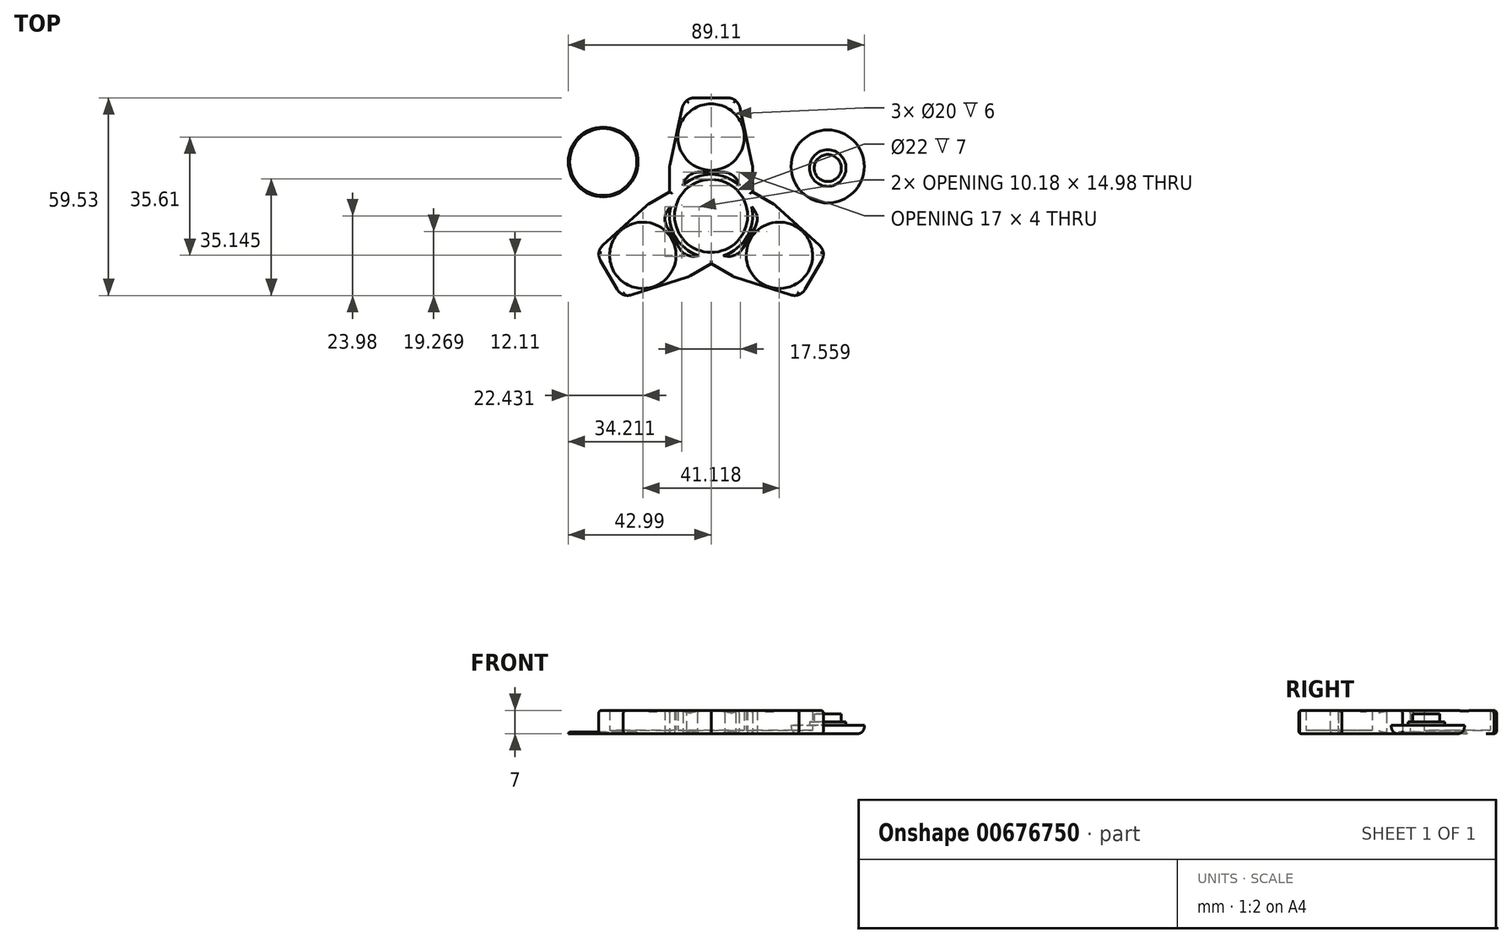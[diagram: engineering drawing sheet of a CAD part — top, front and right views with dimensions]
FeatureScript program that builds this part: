
annotation { "Feature Type Name" : "Feature", "Feature Type Description" : "" }
export const myFeature = defineFeature(function(context is Context, id is Id, definition is map)
    precondition{}
    {
        {
            var Q0;
            Q0=qCreatedBy(makeId("Top.planeOp"),FACE);
            var sketch = newSketch(context, id + "F0", { "sketchPlane" : qUnion([Q0])});
            skCircle(sketch, "E0", {"center": v(0, 0) * mm, "radius": 11 * mm});
            skCircle(sketch, "E1", {"center": v(0, 0) * mm, "radius": 12.5 * mm});
            skLineSegment(sketch, "E2", {"start": v(-8.5, 9.17) * mm, "end": v(-8.5, 13.17) * mm});
            skLineSegment(sketch, "E3", {"start": v(-8.5, 13.17) * mm, "end": v(8.5, 13.17) * mm});
            skLineSegment(sketch, "E4", {"start": v(8.5, 13.17) * mm, "end": v(8.5, 9.17) * mm});
            skLineSegment(sketch, "E5", {"start": v(-12.5, 0) * mm, "end": v(-12.5, 14.98) * mm});
            skLineSegment(sketch, "E6", {"start": v(12.5, 0) * mm, "end": v(12.5, 14.98) * mm});
            skLineSegment(sketch, "E7", {"start": v(0, 35.55) * mm, "end": v(8, 35.55) * mm});
            skPoint(sketch, "E7.startSnap0", {"position": v(0, 13.17) * mm});
            skLineSegment(sketch, "E8", {"start": v(0, 35.55) * mm, "end": v(-8, 35.55) * mm});
            skLineSegment(sketch, "E9", {"start": v(-8, 35.55) * mm, "end": v(-12.5, 14.98) * mm});
            skLineSegment(sketch, "E10", {"start": v(8, 35.55) * mm, "end": v(12.5, 14.98) * mm});
            skCircle(sketch, "E11", {"center": v(0, 23.74) * mm, "radius": 10 * mm});
            skSolve(sketch);
        }
        {
            var Q0;
            Q0=makeQuery(id+"F0.imprint","IMPRINT",FACE,{"disambiguationData":[TD([[makeQuery(id+"F0.imprint","IMPRINT",EDGE,{"derivedFrom":sQuery(id+"F0.wireOp",EDGE,"E0")}),-1.0]])]});
            extrude(context, id + "F1", {"entities" : qUnion([Q0]), "depth" : 7 * mm, "offsetDistance" : 25 * mm});
        }
        {
            var Q0;
            {var subQ4=sQuery(id+"F0.wireOp",EDGE,"E2");Q0=makeQuery(id+"F0.imprint","IMPRINT",FACE,{"disambiguationData":[TD([[makeQuery(id+"F0.imprint","IMPRINT",EDGE,{"derivedFrom":subQ4}),1.0]])]});}
            extrude(context, id + "F2", {"entities" : qUnion([Q0]), "depth" : 7 * mm, "offsetDistance" : 25 * mm});
        }
        {
            var Q0;
            Q0=makeQuery(id+"F0.imprint","IMPRINT",FACE,{"disambiguationData":[TD([[makeQuery(id+"F0.imprint","IMPRINT",EDGE,{"derivedFrom":sQuery(id+"F0.wireOp",EDGE,"E11")}),1.0]])]});
            extrude(context, id + "F3", {"entities" : qUnion([Q0]), "operationType" : NewBodyOperationType.ADD, "depth" : 1 * mm, "offsetDistance" : 25 * mm});
        }
        {
            var Q0;
            Q0=makeQuery(id+"F2.opExtrude","SWEPT_EDGE",EDGE,{"disambiguationData":[OSD([sQuery(id+"F0.wireOp",EDGE,"E7"),sQuery(id+"F0.wireOp",EDGE,"E10")])]});
            var Q1;
            Q1=makeQuery(id+"F2.opExtrude","SWEPT_EDGE",EDGE,{"disambiguationData":[OSD([sQuery(id+"F0.wireOp",EDGE,"E8"),sQuery(id+"F0.wireOp",EDGE,"E9")])]});
            chamfer(context, id + "F4", {"entities" : qUnion([Q0, Q1]), "width" : 2 * mm, "tangentPropagation" : true});
        }
        {
            var Q0;
            {var subQ0=sQuery(id+"F0.wireOp",EDGE,"E10");Q0=makeQuery(id+"F4.opChamfer","BLEND_EDGE",EDGE,{"blendedFrom":[makeQuery(id+"F2.opExtrude","SWEPT_EDGE",EDGE,{"disambiguationData":[OSD([sQuery(id+"F0.wireOp",EDGE,"E7"),subQ0])]}),makeQuery(id+"F2.opExtrude","SWEPT_FACE",FACE,{"disambiguationData":[OSD([subQ0])]})],"blendedInto":[makeQuery(id+"F2.opExtrude","SWEPT_FACE",FACE,{"disambiguationData":[OSD([subQ0])]})]});}
            var Q1;
            {var subQ0=sQuery(id+"F0.wireOp",EDGE,"E7");Q1=makeQuery(id+"F4.opChamfer","BLEND_EDGE",EDGE,{"blendedFrom":[makeQuery(id+"F2.opExtrude","SWEPT_EDGE",EDGE,{"disambiguationData":[OSD([subQ0,sQuery(id+"F0.wireOp",EDGE,"E10")])]}),makeQuery(id+"F2.opExtrude","SWEPT_FACE",FACE,{"disambiguationData":[OSD([subQ0,sQuery(id+"F0.wireOp",EDGE,"E8")])]})],"blendedInto":[makeQuery(id+"F2.opExtrude","SWEPT_FACE",FACE,{"disambiguationData":[OSD([subQ0,sQuery(id+"F0.wireOp",EDGE,"E8")])]})]});}
            var Q2;
            {var subQ0=sQuery(id+"F0.wireOp",EDGE,"E8");Q2=makeQuery(id+"F4.opChamfer","BLEND_EDGE",EDGE,{"blendedFrom":[makeQuery(id+"F2.opExtrude","SWEPT_EDGE",EDGE,{"disambiguationData":[OSD([subQ0,sQuery(id+"F0.wireOp",EDGE,"E9")])]}),makeQuery(id+"F2.opExtrude","SWEPT_FACE",FACE,{"disambiguationData":[OSD([sQuery(id+"F0.wireOp",EDGE,"E7"),subQ0])]})],"blendedInto":[makeQuery(id+"F2.opExtrude","SWEPT_FACE",FACE,{"disambiguationData":[OSD([sQuery(id+"F0.wireOp",EDGE,"E7"),subQ0])]})]});}
            var Q3;
            {var subQ0=sQuery(id+"F0.wireOp",EDGE,"E9");Q3=makeQuery(id+"F4.opChamfer","BLEND_EDGE",EDGE,{"blendedFrom":[makeQuery(id+"F2.opExtrude","SWEPT_EDGE",EDGE,{"disambiguationData":[OSD([sQuery(id+"F0.wireOp",EDGE,"E8"),subQ0])]}),makeQuery(id+"F2.opExtrude","SWEPT_FACE",FACE,{"disambiguationData":[OSD([subQ0])]})],"blendedInto":[makeQuery(id+"F2.opExtrude","SWEPT_FACE",FACE,{"disambiguationData":[OSD([subQ0])]})]});}
            var Q4;
            Q4=makeQuery(id+"F2.opExtrude","SWEPT_EDGE",EDGE,{"disambiguationData":[OSD([sQuery(id+"F0.wireOp",EDGE,"E5"),sQuery(id+"F0.wireOp",EDGE,"E9")])]});
            var Q5;
            Q5=makeQuery(id+"F2.opExtrude","SWEPT_EDGE",EDGE,{"disambiguationData":[OSD([sQuery(id+"F0.wireOp",EDGE,"E6"),sQuery(id+"F0.wireOp",EDGE,"E10")])]});
            fillet(context, id + "F5", {"entities" : qUnion([Q0, Q1, Q2, Q3, Q4, Q5]), "radius" : 4 * mm, "tangentPropagation" : true, "allowEdgeOverflow" : false});
        }
        {
            var Q0;
            Q0=makeQuery(id+"F2.opExtrude","CAP_EDGE",EDGE,{"disambiguationData":[OSD([sQuery(id+"F0.wireOp",EDGE,"E10")])],"isStart":false});
            var Q1;
            {var subQ0=sQuery(id+"F0.wireOp",EDGE,"E10");var subQ1=sQuery(id+"F0.wireOp",EDGE,"E7");Q1=makeQuery(id+"F5.opFillet","BLEND_EDGE",EDGE,{"blendedFrom":[makeQuery(id+"F4.opChamfer","BLEND_EDGE",EDGE,{"blendedFrom":[makeQuery(id+"F2.opExtrude","SWEPT_EDGE",EDGE,{"disambiguationData":[OSD([subQ1,subQ0])]}),makeQuery(id+"F2.opExtrude","SWEPT_FACE",FACE,{"disambiguationData":[OSD([subQ0])]})],"blendedInto":[makeQuery(id+"F2.opExtrude","SWEPT_FACE",FACE,{"disambiguationData":[OSD([subQ0])]})]}),makeQuery(id+"F2.opExtrude","CAP_FACE",FACE,{"disambiguationData":[OSD([sQuery(id+"F0.wireOp",EDGE,"E1"),sQuery(id+"F0.wireOp",EDGE,"E2"),sQuery(id+"F0.wireOp",EDGE,"E3"),sQuery(id+"F0.wireOp",EDGE,"E4"),sQuery(id+"F0.wireOp",EDGE,"E5"),sQuery(id+"F0.wireOp",EDGE,"E6"),subQ1,sQuery(id+"F0.wireOp",EDGE,"E8"),sQuery(id+"F0.wireOp",EDGE,"E9"),subQ0,sQuery(id+"F0.wireOp",EDGE,"E11")])],"isStart":false})],"blendedInto":[makeQuery(id+"F2.opExtrude","CAP_FACE",FACE,{"disambiguationData":[OSD([sQuery(id+"F0.wireOp",EDGE,"E1"),sQuery(id+"F0.wireOp",EDGE,"E2"),sQuery(id+"F0.wireOp",EDGE,"E3"),sQuery(id+"F0.wireOp",EDGE,"E4"),sQuery(id+"F0.wireOp",EDGE,"E5"),sQuery(id+"F0.wireOp",EDGE,"E6"),subQ1,sQuery(id+"F0.wireOp",EDGE,"E8"),sQuery(id+"F0.wireOp",EDGE,"E9"),subQ0,sQuery(id+"F0.wireOp",EDGE,"E11")])],"isStart":false})]});}
            var Q2;
            {var subQ0=sQuery(id+"F0.wireOp",EDGE,"E10");var subQ1=sQuery(id+"F0.wireOp",EDGE,"E8");var subQ2=sQuery(id+"F0.wireOp",EDGE,"E7");Q2=makeQuery(id+"F5.opFillet","BLEND_EDGE",EDGE,{"blendedFrom":[makeQuery(id+"F4.opChamfer","BLEND_EDGE",EDGE,{"blendedFrom":[makeQuery(id+"F2.opExtrude","SWEPT_EDGE",EDGE,{"disambiguationData":[OSD([subQ2,subQ0])]}),makeQuery(id+"F2.opExtrude","SWEPT_FACE",FACE,{"disambiguationData":[OSD([subQ2,subQ1])]})],"blendedInto":[makeQuery(id+"F2.opExtrude","SWEPT_FACE",FACE,{"disambiguationData":[OSD([subQ2,subQ1])]})]}),makeQuery(id+"F2.opExtrude","CAP_FACE",FACE,{"disambiguationData":[OSD([sQuery(id+"F0.wireOp",EDGE,"E1"),sQuery(id+"F0.wireOp",EDGE,"E2"),sQuery(id+"F0.wireOp",EDGE,"E3"),sQuery(id+"F0.wireOp",EDGE,"E4"),sQuery(id+"F0.wireOp",EDGE,"E5"),sQuery(id+"F0.wireOp",EDGE,"E6"),subQ2,subQ1,sQuery(id+"F0.wireOp",EDGE,"E9"),subQ0,sQuery(id+"F0.wireOp",EDGE,"E11")])],"isStart":false})],"blendedInto":[makeQuery(id+"F2.opExtrude","CAP_FACE",FACE,{"disambiguationData":[OSD([sQuery(id+"F0.wireOp",EDGE,"E1"),sQuery(id+"F0.wireOp",EDGE,"E2"),sQuery(id+"F0.wireOp",EDGE,"E3"),sQuery(id+"F0.wireOp",EDGE,"E4"),sQuery(id+"F0.wireOp",EDGE,"E5"),sQuery(id+"F0.wireOp",EDGE,"E6"),subQ2,subQ1,sQuery(id+"F0.wireOp",EDGE,"E9"),subQ0,sQuery(id+"F0.wireOp",EDGE,"E11")])],"isStart":false})]});}
            var Q3;
            Q3=makeQuery(id+"F2.opExtrude","CAP_EDGE",EDGE,{"disambiguationData":[OSD([sQuery(id+"F0.wireOp",EDGE,"E7"),sQuery(id+"F0.wireOp",EDGE,"E8")])],"isStart":false});
            var Q4;
            {var subQ0=sQuery(id+"F0.wireOp",EDGE,"E9");var subQ1=sQuery(id+"F0.wireOp",EDGE,"E8");Q4=makeQuery(id+"F4.opChamfer","BLEND_EDGE",EDGE,{"blendedFrom":[makeQuery(id+"F2.opExtrude","SWEPT_EDGE",EDGE,{"disambiguationData":[OSD([subQ1,subQ0])]}),makeQuery(id+"F2.opExtrude","CAP_FACE",FACE,{"disambiguationData":[OSD([sQuery(id+"F0.wireOp",EDGE,"E1"),sQuery(id+"F0.wireOp",EDGE,"E2"),sQuery(id+"F0.wireOp",EDGE,"E3"),sQuery(id+"F0.wireOp",EDGE,"E4"),sQuery(id+"F0.wireOp",EDGE,"E5"),sQuery(id+"F0.wireOp",EDGE,"E6"),sQuery(id+"F0.wireOp",EDGE,"E7"),subQ1,subQ0,sQuery(id+"F0.wireOp",EDGE,"E10"),sQuery(id+"F0.wireOp",EDGE,"E11")])],"isStart":false})],"blendedInto":[makeQuery(id+"F2.opExtrude","CAP_FACE",FACE,{"disambiguationData":[OSD([sQuery(id+"F0.wireOp",EDGE,"E1"),sQuery(id+"F0.wireOp",EDGE,"E2"),sQuery(id+"F0.wireOp",EDGE,"E3"),sQuery(id+"F0.wireOp",EDGE,"E4"),sQuery(id+"F0.wireOp",EDGE,"E5"),sQuery(id+"F0.wireOp",EDGE,"E6"),sQuery(id+"F0.wireOp",EDGE,"E7"),subQ1,subQ0,sQuery(id+"F0.wireOp",EDGE,"E10"),sQuery(id+"F0.wireOp",EDGE,"E11")])],"isStart":false})]});}
            var Q5;
            {var subQ0=sQuery(id+"F0.wireOp",EDGE,"E9");var subQ1=sQuery(id+"F0.wireOp",EDGE,"E8");var subQ2=sQuery(id+"F0.wireOp",EDGE,"E7");Q5=makeQuery(id+"F5.opFillet","BLEND_EDGE",EDGE,{"blendedFrom":[makeQuery(id+"F4.opChamfer","BLEND_EDGE",EDGE,{"blendedFrom":[makeQuery(id+"F2.opExtrude","SWEPT_EDGE",EDGE,{"disambiguationData":[OSD([subQ1,subQ0])]}),makeQuery(id+"F2.opExtrude","SWEPT_FACE",FACE,{"disambiguationData":[OSD([subQ2,subQ1])]})],"blendedInto":[makeQuery(id+"F2.opExtrude","SWEPT_FACE",FACE,{"disambiguationData":[OSD([subQ2,subQ1])]})]}),makeQuery(id+"F2.opExtrude","CAP_FACE",FACE,{"disambiguationData":[OSD([sQuery(id+"F0.wireOp",EDGE,"E1"),sQuery(id+"F0.wireOp",EDGE,"E2"),sQuery(id+"F0.wireOp",EDGE,"E3"),sQuery(id+"F0.wireOp",EDGE,"E4"),sQuery(id+"F0.wireOp",EDGE,"E5"),sQuery(id+"F0.wireOp",EDGE,"E6"),subQ2,subQ1,subQ0,sQuery(id+"F0.wireOp",EDGE,"E10"),sQuery(id+"F0.wireOp",EDGE,"E11")])],"isStart":false})],"blendedInto":[makeQuery(id+"F2.opExtrude","CAP_FACE",FACE,{"disambiguationData":[OSD([sQuery(id+"F0.wireOp",EDGE,"E1"),sQuery(id+"F0.wireOp",EDGE,"E2"),sQuery(id+"F0.wireOp",EDGE,"E3"),sQuery(id+"F0.wireOp",EDGE,"E4"),sQuery(id+"F0.wireOp",EDGE,"E5"),sQuery(id+"F0.wireOp",EDGE,"E6"),subQ2,subQ1,subQ0,sQuery(id+"F0.wireOp",EDGE,"E10"),sQuery(id+"F0.wireOp",EDGE,"E11")])],"isStart":false})]});}
            var Q6;
            {var subQ0=sQuery(id+"F0.wireOp",EDGE,"E9");var subQ1=sQuery(id+"F0.wireOp",EDGE,"E8");Q6=makeQuery(id+"F5.opFillet","BLEND_EDGE",EDGE,{"blendedFrom":[makeQuery(id+"F4.opChamfer","BLEND_EDGE",EDGE,{"blendedFrom":[makeQuery(id+"F2.opExtrude","SWEPT_EDGE",EDGE,{"disambiguationData":[OSD([subQ1,subQ0])]}),makeQuery(id+"F2.opExtrude","SWEPT_FACE",FACE,{"disambiguationData":[OSD([subQ0])]})],"blendedInto":[makeQuery(id+"F2.opExtrude","SWEPT_FACE",FACE,{"disambiguationData":[OSD([subQ0])]})]}),makeQuery(id+"F2.opExtrude","CAP_FACE",FACE,{"disambiguationData":[OSD([sQuery(id+"F0.wireOp",EDGE,"E1"),sQuery(id+"F0.wireOp",EDGE,"E2"),sQuery(id+"F0.wireOp",EDGE,"E3"),sQuery(id+"F0.wireOp",EDGE,"E4"),sQuery(id+"F0.wireOp",EDGE,"E5"),sQuery(id+"F0.wireOp",EDGE,"E6"),sQuery(id+"F0.wireOp",EDGE,"E7"),subQ1,subQ0,sQuery(id+"F0.wireOp",EDGE,"E10"),sQuery(id+"F0.wireOp",EDGE,"E11")])],"isStart":false})],"blendedInto":[makeQuery(id+"F2.opExtrude","CAP_FACE",FACE,{"disambiguationData":[OSD([sQuery(id+"F0.wireOp",EDGE,"E1"),sQuery(id+"F0.wireOp",EDGE,"E2"),sQuery(id+"F0.wireOp",EDGE,"E3"),sQuery(id+"F0.wireOp",EDGE,"E4"),sQuery(id+"F0.wireOp",EDGE,"E5"),sQuery(id+"F0.wireOp",EDGE,"E6"),sQuery(id+"F0.wireOp",EDGE,"E7"),subQ1,subQ0,sQuery(id+"F0.wireOp",EDGE,"E10"),sQuery(id+"F0.wireOp",EDGE,"E11")])],"isStart":false})]});}
            var Q7;
            Q7=makeQuery(id+"F2.opExtrude","CAP_EDGE",EDGE,{"disambiguationData":[OSD([sQuery(id+"F0.wireOp",EDGE,"E9")])],"isStart":false});
            var Q8;
            {var subQ0=sQuery(id+"F0.wireOp",EDGE,"E10");var subQ1=sQuery(id+"F0.wireOp",EDGE,"E6");Q8=makeQuery(id+"F5.opFillet","BLEND_EDGE",EDGE,{"blendedFrom":[makeQuery(id+"F2.opExtrude","SWEPT_EDGE",EDGE,{"disambiguationData":[OSD([subQ1,subQ0])]}),makeQuery(id+"F2.opExtrude","CAP_FACE",FACE,{"disambiguationData":[OSD([sQuery(id+"F0.wireOp",EDGE,"E1"),sQuery(id+"F0.wireOp",EDGE,"E2"),sQuery(id+"F0.wireOp",EDGE,"E3"),sQuery(id+"F0.wireOp",EDGE,"E4"),sQuery(id+"F0.wireOp",EDGE,"E5"),subQ1,sQuery(id+"F0.wireOp",EDGE,"E7"),sQuery(id+"F0.wireOp",EDGE,"E8"),sQuery(id+"F0.wireOp",EDGE,"E9"),subQ0,sQuery(id+"F0.wireOp",EDGE,"E11")])],"isStart":false})],"blendedInto":[makeQuery(id+"F2.opExtrude","CAP_FACE",FACE,{"disambiguationData":[OSD([sQuery(id+"F0.wireOp",EDGE,"E1"),sQuery(id+"F0.wireOp",EDGE,"E2"),sQuery(id+"F0.wireOp",EDGE,"E3"),sQuery(id+"F0.wireOp",EDGE,"E4"),sQuery(id+"F0.wireOp",EDGE,"E5"),subQ1,sQuery(id+"F0.wireOp",EDGE,"E7"),sQuery(id+"F0.wireOp",EDGE,"E8"),sQuery(id+"F0.wireOp",EDGE,"E9"),subQ0,sQuery(id+"F0.wireOp",EDGE,"E11")])],"isStart":false})]});}
            var Q9;
            {var subQ0=sQuery(id+"F0.wireOp",EDGE,"E11");var subQ1=sQuery(id+"F0.wireOp",EDGE,"E10");var subQ2=sQuery(id+"F0.wireOp",EDGE,"E8");var subQ3=sQuery(id+"F0.wireOp",EDGE,"E7");Q9=makeQuery(id+"F5.opFillet","BLEND_EDGE",EDGE,{"blendedFrom":[makeQuery(id+"F4.opChamfer","BLEND_EDGE",EDGE,{"blendedFrom":[makeQuery(id+"F2.opExtrude","SWEPT_EDGE",EDGE,{"disambiguationData":[OSD([subQ3,subQ1])]}),makeQuery(id+"F2.opExtrude","SWEPT_FACE",FACE,{"disambiguationData":[OSD([subQ3,subQ2])]})],"blendedInto":[makeQuery(id+"F2.opExtrude","SWEPT_FACE",FACE,{"disambiguationData":[OSD([subQ3,subQ2])]})]}),makeQuery(id+"F3.boolean.opBoolean","MERGE",FACE,{"derivedFrom":[makeQuery(id+"F2.opExtrude","CAP_FACE",FACE,{"disambiguationData":[OSD([sQuery(id+"F0.wireOp",EDGE,"E1"),sQuery(id+"F0.wireOp",EDGE,"E2"),sQuery(id+"F0.wireOp",EDGE,"E3"),sQuery(id+"F0.wireOp",EDGE,"E4"),sQuery(id+"F0.wireOp",EDGE,"E5"),sQuery(id+"F0.wireOp",EDGE,"E6"),subQ3,subQ2,sQuery(id+"F0.wireOp",EDGE,"E9"),subQ1,subQ0])],"isStart":true}),makeQuery(id+"F3.opExtrude","CAP_FACE",FACE,{"disambiguationData":[OSD([subQ0])],"isStart":true})]})],"blendedInto":[makeQuery(id+"F3.boolean.opBoolean","MERGE",FACE,{"derivedFrom":[makeQuery(id+"F2.opExtrude","CAP_FACE",FACE,{"disambiguationData":[OSD([sQuery(id+"F0.wireOp",EDGE,"E1"),sQuery(id+"F0.wireOp",EDGE,"E2"),sQuery(id+"F0.wireOp",EDGE,"E3"),sQuery(id+"F0.wireOp",EDGE,"E4"),sQuery(id+"F0.wireOp",EDGE,"E5"),sQuery(id+"F0.wireOp",EDGE,"E6"),subQ3,subQ2,sQuery(id+"F0.wireOp",EDGE,"E9"),subQ1,subQ0])],"isStart":true}),makeQuery(id+"F3.opExtrude","CAP_FACE",FACE,{"disambiguationData":[OSD([subQ0])],"isStart":true})]})]});}
            var Q10;
            {var subQ0=sQuery(id+"F0.wireOp",EDGE,"E11");var subQ1=sQuery(id+"F0.wireOp",EDGE,"E10");var subQ2=sQuery(id+"F0.wireOp",EDGE,"E7");Q10=makeQuery(id+"F5.opFillet","BLEND_EDGE",EDGE,{"blendedFrom":[makeQuery(id+"F4.opChamfer","BLEND_EDGE",EDGE,{"blendedFrom":[makeQuery(id+"F2.opExtrude","SWEPT_EDGE",EDGE,{"disambiguationData":[OSD([subQ2,subQ1])]}),makeQuery(id+"F2.opExtrude","SWEPT_FACE",FACE,{"disambiguationData":[OSD([subQ1])]})],"blendedInto":[makeQuery(id+"F2.opExtrude","SWEPT_FACE",FACE,{"disambiguationData":[OSD([subQ1])]})]}),makeQuery(id+"F3.boolean.opBoolean","MERGE",FACE,{"derivedFrom":[makeQuery(id+"F2.opExtrude","CAP_FACE",FACE,{"disambiguationData":[OSD([sQuery(id+"F0.wireOp",EDGE,"E1"),sQuery(id+"F0.wireOp",EDGE,"E2"),sQuery(id+"F0.wireOp",EDGE,"E3"),sQuery(id+"F0.wireOp",EDGE,"E4"),sQuery(id+"F0.wireOp",EDGE,"E5"),sQuery(id+"F0.wireOp",EDGE,"E6"),subQ2,sQuery(id+"F0.wireOp",EDGE,"E8"),sQuery(id+"F0.wireOp",EDGE,"E9"),subQ1,subQ0])],"isStart":true}),makeQuery(id+"F3.opExtrude","CAP_FACE",FACE,{"disambiguationData":[OSD([subQ0])],"isStart":true})]})],"blendedInto":[makeQuery(id+"F3.boolean.opBoolean","MERGE",FACE,{"derivedFrom":[makeQuery(id+"F2.opExtrude","CAP_FACE",FACE,{"disambiguationData":[OSD([sQuery(id+"F0.wireOp",EDGE,"E1"),sQuery(id+"F0.wireOp",EDGE,"E2"),sQuery(id+"F0.wireOp",EDGE,"E3"),sQuery(id+"F0.wireOp",EDGE,"E4"),sQuery(id+"F0.wireOp",EDGE,"E5"),sQuery(id+"F0.wireOp",EDGE,"E6"),subQ2,sQuery(id+"F0.wireOp",EDGE,"E8"),sQuery(id+"F0.wireOp",EDGE,"E9"),subQ1,subQ0])],"isStart":true}),makeQuery(id+"F3.opExtrude","CAP_FACE",FACE,{"disambiguationData":[OSD([subQ0])],"isStart":true})]})]});}
            var Q11;
            Q11=makeQuery(id+"F2.opExtrude","CAP_EDGE",EDGE,{"disambiguationData":[OSD([sQuery(id+"F0.wireOp",EDGE,"E10")])],"isStart":true});
            var Q12;
            Q12=makeQuery(id+"F2.opExtrude","CAP_EDGE",EDGE,{"disambiguationData":[OSD([sQuery(id+"F0.wireOp",EDGE,"E7"),sQuery(id+"F0.wireOp",EDGE,"E8")])],"isStart":true});
            var Q13;
            {var subQ0=sQuery(id+"F0.wireOp",EDGE,"E11");var subQ1=sQuery(id+"F0.wireOp",EDGE,"E9");var subQ2=sQuery(id+"F0.wireOp",EDGE,"E8");var subQ3=sQuery(id+"F0.wireOp",EDGE,"E7");Q13=makeQuery(id+"F5.opFillet","BLEND_EDGE",EDGE,{"blendedFrom":[makeQuery(id+"F4.opChamfer","BLEND_EDGE",EDGE,{"blendedFrom":[makeQuery(id+"F2.opExtrude","SWEPT_EDGE",EDGE,{"disambiguationData":[OSD([subQ2,subQ1])]}),makeQuery(id+"F2.opExtrude","SWEPT_FACE",FACE,{"disambiguationData":[OSD([subQ3,subQ2])]})],"blendedInto":[makeQuery(id+"F2.opExtrude","SWEPT_FACE",FACE,{"disambiguationData":[OSD([subQ3,subQ2])]})]}),makeQuery(id+"F3.boolean.opBoolean","MERGE",FACE,{"derivedFrom":[makeQuery(id+"F2.opExtrude","CAP_FACE",FACE,{"disambiguationData":[OSD([sQuery(id+"F0.wireOp",EDGE,"E1"),sQuery(id+"F0.wireOp",EDGE,"E2"),sQuery(id+"F0.wireOp",EDGE,"E3"),sQuery(id+"F0.wireOp",EDGE,"E4"),sQuery(id+"F0.wireOp",EDGE,"E5"),sQuery(id+"F0.wireOp",EDGE,"E6"),subQ3,subQ2,subQ1,sQuery(id+"F0.wireOp",EDGE,"E10"),subQ0])],"isStart":true}),makeQuery(id+"F3.opExtrude","CAP_FACE",FACE,{"disambiguationData":[OSD([subQ0])],"isStart":true})]})],"blendedInto":[makeQuery(id+"F3.boolean.opBoolean","MERGE",FACE,{"derivedFrom":[makeQuery(id+"F2.opExtrude","CAP_FACE",FACE,{"disambiguationData":[OSD([sQuery(id+"F0.wireOp",EDGE,"E1"),sQuery(id+"F0.wireOp",EDGE,"E2"),sQuery(id+"F0.wireOp",EDGE,"E3"),sQuery(id+"F0.wireOp",EDGE,"E4"),sQuery(id+"F0.wireOp",EDGE,"E5"),sQuery(id+"F0.wireOp",EDGE,"E6"),subQ3,subQ2,subQ1,sQuery(id+"F0.wireOp",EDGE,"E10"),subQ0])],"isStart":true}),makeQuery(id+"F3.opExtrude","CAP_FACE",FACE,{"disambiguationData":[OSD([subQ0])],"isStart":true})]})]});}
            var Q14;
            {var subQ0=sQuery(id+"F0.wireOp",EDGE,"E11");var subQ1=sQuery(id+"F0.wireOp",EDGE,"E9");var subQ2=sQuery(id+"F0.wireOp",EDGE,"E8");Q14=makeQuery(id+"F5.opFillet","BLEND_EDGE",EDGE,{"blendedFrom":[makeQuery(id+"F4.opChamfer","BLEND_EDGE",EDGE,{"blendedFrom":[makeQuery(id+"F2.opExtrude","SWEPT_EDGE",EDGE,{"disambiguationData":[OSD([subQ2,subQ1])]}),makeQuery(id+"F2.opExtrude","SWEPT_FACE",FACE,{"disambiguationData":[OSD([subQ1])]})],"blendedInto":[makeQuery(id+"F2.opExtrude","SWEPT_FACE",FACE,{"disambiguationData":[OSD([subQ1])]})]}),makeQuery(id+"F3.boolean.opBoolean","MERGE",FACE,{"derivedFrom":[makeQuery(id+"F2.opExtrude","CAP_FACE",FACE,{"disambiguationData":[OSD([sQuery(id+"F0.wireOp",EDGE,"E1"),sQuery(id+"F0.wireOp",EDGE,"E2"),sQuery(id+"F0.wireOp",EDGE,"E3"),sQuery(id+"F0.wireOp",EDGE,"E4"),sQuery(id+"F0.wireOp",EDGE,"E5"),sQuery(id+"F0.wireOp",EDGE,"E6"),sQuery(id+"F0.wireOp",EDGE,"E7"),subQ2,subQ1,sQuery(id+"F0.wireOp",EDGE,"E10"),subQ0])],"isStart":true}),makeQuery(id+"F3.opExtrude","CAP_FACE",FACE,{"disambiguationData":[OSD([subQ0])],"isStart":true})]})],"blendedInto":[makeQuery(id+"F3.boolean.opBoolean","MERGE",FACE,{"derivedFrom":[makeQuery(id+"F2.opExtrude","CAP_FACE",FACE,{"disambiguationData":[OSD([sQuery(id+"F0.wireOp",EDGE,"E1"),sQuery(id+"F0.wireOp",EDGE,"E2"),sQuery(id+"F0.wireOp",EDGE,"E3"),sQuery(id+"F0.wireOp",EDGE,"E4"),sQuery(id+"F0.wireOp",EDGE,"E5"),sQuery(id+"F0.wireOp",EDGE,"E6"),sQuery(id+"F0.wireOp",EDGE,"E7"),subQ2,subQ1,sQuery(id+"F0.wireOp",EDGE,"E10"),subQ0])],"isStart":true}),makeQuery(id+"F3.opExtrude","CAP_FACE",FACE,{"disambiguationData":[OSD([subQ0])],"isStart":true})]})]});}
            var Q15;
            Q15=makeQuery(id+"F2.opExtrude","CAP_EDGE",EDGE,{"disambiguationData":[OSD([sQuery(id+"F0.wireOp",EDGE,"E9")])],"isStart":true});
            var Q16;
            {var subQ0=sQuery(id+"F0.wireOp",EDGE,"E11");var subQ1=sQuery(id+"F0.wireOp",EDGE,"E9");var subQ2=sQuery(id+"F0.wireOp",EDGE,"E8");Q16=makeQuery(id+"F4.opChamfer","BLEND_EDGE",EDGE,{"blendedFrom":[makeQuery(id+"F2.opExtrude","SWEPT_EDGE",EDGE,{"disambiguationData":[OSD([subQ2,subQ1])]}),makeQuery(id+"F3.boolean.opBoolean","MERGE",FACE,{"derivedFrom":[makeQuery(id+"F2.opExtrude","CAP_FACE",FACE,{"disambiguationData":[OSD([sQuery(id+"F0.wireOp",EDGE,"E1"),sQuery(id+"F0.wireOp",EDGE,"E2"),sQuery(id+"F0.wireOp",EDGE,"E3"),sQuery(id+"F0.wireOp",EDGE,"E4"),sQuery(id+"F0.wireOp",EDGE,"E5"),sQuery(id+"F0.wireOp",EDGE,"E6"),sQuery(id+"F0.wireOp",EDGE,"E7"),subQ2,subQ1,sQuery(id+"F0.wireOp",EDGE,"E10"),subQ0])],"isStart":true}),makeQuery(id+"F3.opExtrude","CAP_FACE",FACE,{"disambiguationData":[OSD([subQ0])],"isStart":true})]})],"blendedInto":[makeQuery(id+"F3.boolean.opBoolean","MERGE",FACE,{"derivedFrom":[makeQuery(id+"F2.opExtrude","CAP_FACE",FACE,{"disambiguationData":[OSD([sQuery(id+"F0.wireOp",EDGE,"E1"),sQuery(id+"F0.wireOp",EDGE,"E2"),sQuery(id+"F0.wireOp",EDGE,"E3"),sQuery(id+"F0.wireOp",EDGE,"E4"),sQuery(id+"F0.wireOp",EDGE,"E5"),sQuery(id+"F0.wireOp",EDGE,"E6"),sQuery(id+"F0.wireOp",EDGE,"E7"),subQ2,subQ1,sQuery(id+"F0.wireOp",EDGE,"E10"),subQ0])],"isStart":true}),makeQuery(id+"F3.opExtrude","CAP_FACE",FACE,{"disambiguationData":[OSD([subQ0])],"isStart":true})]})]});}
            fillet(context, id + "F6", {"entities" : qUnion([Q0, Q1, Q2, Q3, Q4, Q5, Q6, Q7, Q8, Q9, Q10, Q11, Q12, Q13, Q14, Q15, Q16]), "radius" : .8 * mm, "tangentPropagation" : true, "allowEdgeOverflow" : false});
        }
        {
            var Q0;
            Q0=makeQuery(id+"F2.opExtrude","SWEPT_EDGE",EDGE,{"disambiguationData":[OSD([sQuery(id+"F0.wireOp",EDGE,"E2"),sQuery(id+"F0.wireOp",EDGE,"E3")])]});
            var Q1;
            Q1=makeQuery(id+"F2.opExtrude","SWEPT_EDGE",EDGE,{"disambiguationData":[OSD([sQuery(id+"F0.wireOp",EDGE,"E3"),sQuery(id+"F0.wireOp",EDGE,"E4")])]});
            fillet(context, id + "F7", {"entities" : qUnion([Q0, Q1]), "radius" : 5 * mm, "tangentPropagation" : true, "allowEdgeOverflow" : false});
        }
        {
            var Q0;
            Q0=makeQuery(id+"F2.opExtrude","SWEPT_BODY",BODY,{"disambiguationData":[OSD([sQuery(id+"F0.wireOp",EDGE,"E1"),sQuery(id+"F0.wireOp",EDGE,"E2"),sQuery(id+"F0.wireOp",EDGE,"E3"),sQuery(id+"F0.wireOp",EDGE,"E4"),sQuery(id+"F0.wireOp",EDGE,"E5"),sQuery(id+"F0.wireOp",EDGE,"E6"),sQuery(id+"F0.wireOp",EDGE,"E7"),sQuery(id+"F0.wireOp",EDGE,"E8"),sQuery(id+"F0.wireOp",EDGE,"E9"),sQuery(id+"F0.wireOp",EDGE,"E10"),sQuery(id+"F0.wireOp",EDGE,"E11")])]});
            var Q1;
            Q1=makeQuery(id+"F1.opExtrude","CAP_EDGE",EDGE,{"disambiguationData":[OSD([sQuery(id+"F0.wireOp",EDGE,"E0")])],"isStart":false});
            circularPattern(context, id + "F8", {"operationType" : NewBodyOperationType.ADD, "entities" : qUnion([Q0]), "axis" : qUnion([Q1]), "angle" : 360 * degree, "instanceCount" : 3, "equalSpace" : true});
        }
        {
            var Q0;
            Q0=qCreatedBy(makeId("Top.planeOp"),FACE);
            var sketch = newSketch(context, id + "F9", { "sketchPlane" : qUnion([Q0])});
            skCircle(sketch, "E12", {"center": v(-32.5, 16.25) * mm, "radius": 10.5 * mm});
            skSolve(sketch);
        }
        {
            var Q0;
            Q0=makeQuery(id+"F9.imprint","IMPRINT",FACE,{"disambiguationData":[TD([[makeQuery(id+"F9.imprint","IMPRINT",EDGE,{"derivedFrom":sQuery(id+"F9.wireOp",EDGE,"E12")}),1.0]])]});
            extrude(context, id + "F10", {"entities" : qUnion([Q0]), "depth" : .5 * mm, "offsetDistance" : 25 * mm});
        }
        {
            var Q0;
            Q0=makeQuery(id+"F10.opExtrude","CAP_FACE",FACE,{"disambiguationData":[OSD([sQuery(id+"F9.wireOp",EDGE,"E12")])],"isStart":false});
            chamfer(context, id + "F11", {"entities" : qUnion([Q0]), "width" : .4 * mm, "tangentPropagation" : true});
        }
        {
            var Q0;
            Q0=qCreatedBy(makeId("Top.planeOp"),FACE);
            var sketch = newSketch(context, id + "F12", { "sketchPlane" : qUnion([Q0])});
            skCircle(sketch, "E13", {"center": v(35.12, 14.41) * mm, "radius": 4.08 * mm});
            skCircle(sketch, "E14", {"center": v(35.12, 14.41) * mm, "radius": 5.5 * mm});
            skCircle(sketch, "E15", {"center": v(35.12, 14.9) * mm, "radius": 11 * mm});
            skSolve(sketch);
        }
        {
            var Q0;
            Q0=makeQuery(id+"F12.imprint","IMPRINT",FACE,{"disambiguationData":[TD([[makeQuery(id+"F12.imprint","IMPRINT",EDGE,{"derivedFrom":sQuery(id+"F12.wireOp",EDGE,"E14")}),-1.0]])]});
            extrude(context, id + "F13", {"entities" : qUnion([Q0]), "depth" : 2.5 * mm, "offsetDistance" : 25 * mm});
        }
        {
            var Q0;
            Q0=makeQuery(id+"F12.imprint","IMPRINT",FACE,{"disambiguationData":[TD([[makeQuery(id+"F12.imprint","IMPRINT",EDGE,{"derivedFrom":sQuery(id+"F12.wireOp",EDGE,"E13")}),-1.0]])]});
            extrude(context, id + "F14", {"entities" : qUnion([Q0]), "operationType" : NewBodyOperationType.ADD, "depth" : 3.5 * mm, "offsetDistance" : 25 * mm});
        }
        {
            var Q0;
            Q0=makeQuery(id+"F12.imprint","IMPRINT",FACE,{"disambiguationData":[TD([[makeQuery(id+"F12.imprint","IMPRINT",EDGE,{"derivedFrom":sQuery(id+"F12.wireOp",EDGE,"E13")}),1.0]])]});
            extrude(context, id + "F15", {"entities" : qUnion([Q0]), "operationType" : NewBodyOperationType.ADD, "depth" : 6 * mm, "offsetDistance" : 25 * mm});
        }
        {
            var Q0;
            Q0=makeQuery(id+"F13.opExtrude","CAP_EDGE",EDGE,{"disambiguationData":[OSD([sQuery(id+"F12.wireOp",EDGE,"E15")])],"isStart":true});
            fillet(context, id + "F16", {"entities" : qUnion([Q0]), "radius" : 2 * mm, "tangentPropagation" : true, "allowEdgeOverflow" : false});
        }
    });
